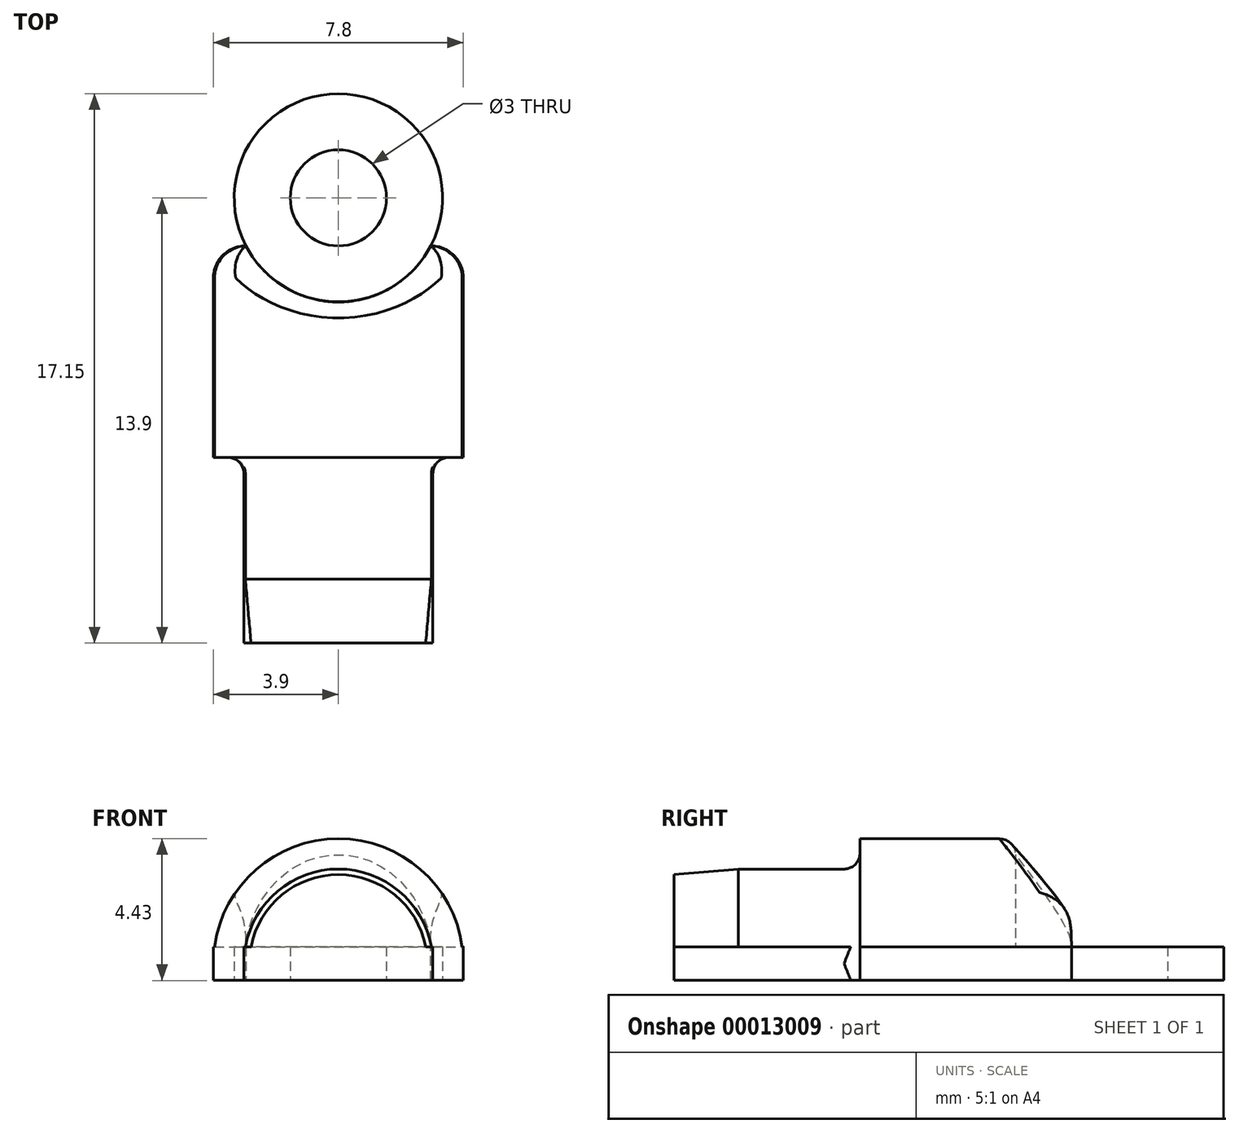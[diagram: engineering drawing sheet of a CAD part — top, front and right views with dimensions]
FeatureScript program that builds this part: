
annotation { "Feature Type Name" : "Feature", "Feature Type Description" : "" }
export const myFeature = defineFeature(function(context is Context, id is Id, definition is map)
    precondition{}
    {
        {
            var Q0;
            Q0=qCreatedBy(makeId("Top.planeOp"),FACE);
            var sketch = newSketch(context, id + "F0", { "sketchPlane" : qUnion([Q0])});
            skArc(sketch, "E0", {"start": v(2.88, -1.5) * mm, "mid": v(0, 3.25) * mm, "end": v(-2.88, -1.5) * mm});
            skCircle(sketch, "E1", {"center": v(0, 0) * mm, "radius": 1.5 * mm});
            skLineSegment(sketch, "E2.bottom", {"start": v(-2.9, -1.5) * mm, "end": v(-2.88, -1.5) * mm});
            skLineSegment(sketch, "E2.top", {"start": v(-3.9, -8.1) * mm, "end": v(-2.95, -8.1) * mm});
            skLineSegment(sketch, "E2.left", {"start": v(-3.9, -2.5) * mm, "end": v(-3.9, -8.1) * mm});
            skLineSegment(sketch, "E2.right", {"start": v(3.9, -2.5) * mm, "end": v(3.9, -8.1) * mm});
            skLineSegment(sketch, "E3.top", {"start": v(-2.95, -13.9) * mm, "end": v(2.95, -13.9) * mm});
            skLineSegment(sketch, "E3.left", {"start": v(-2.95, -8.1) * mm, "end": v(-2.95, -13.9) * mm});
            skLineSegment(sketch, "E3.right", {"start": v(2.95, -8.1) * mm, "end": v(2.95, -13.9) * mm});
            skPoint(sketch, "E4.visualSharp", {"position": v(-3.9, -1.5) * mm});
            skArc(sketch, "E4.filletArc", {"start": v(-2.9, -1.5) * mm, "mid": v(-3.6, -1.8) * mm, "end": v(-3.9, -2.5) * mm});
            skPoint(sketch, "E5.visualSharp", {"position": v(3.9, -1.5) * mm});
            skArc(sketch, "E5.filletArc", {"start": v(3.9, -2.5) * mm, "mid": v(3.6, -1.8) * mm, "end": v(2.9, -1.5) * mm});
            skLineSegment(sketch, "E6.trimOffspring", {"start": v(2.88, -1.5) * mm, "end": v(2.9, -1.5) * mm});
            skLineSegment(sketch, "E7.trimOffspring", {"start": v(2.95, -8.1) * mm, "end": v(3.9, -8.1) * mm});
            skSolve(sketch);
        }
        {
            var Q0;
            Q0=makeQuery(id+"F0.imprint","IMPRINT",FACE,{"disambiguationData":[TD([[makeQuery(id+"F0.imprint","IMPRINT",EDGE,{"derivedFrom":sQuery(id+"F0.wireOp",EDGE,"E0")}),1.0]])]});
            extrude(context, id + "F1", {"entities" : qUnion([Q0]), "endBound" : BoundingType.SYMMETRIC, "depth" : 1.05 * mm});
        }
        {
            var Q0;
            Q0=qCreatedBy(makeId("Top.planeOp"),FACE);
            var sketch = newSketch(context, id + "F2", { "sketchPlane" : qUnion([Q0])});
            skLineSegment(sketch, "E8", {"start": v(0, -13.9) * mm, "end": v(-2.95, -13.9) * mm});
            skLineSegment(sketch, "E9", {"start": v(-2.95, -13.9) * mm, "end": v(-2.95, -8.1) * mm});
            skLineSegment(sketch, "E10", {"start": v(-2.95, -8.1) * mm, "end": v(-3.9, -8.1) * mm});
            skLineSegment(sketch, "E11", {"start": v(-3.9, -8.1) * mm, "end": v(-3.9, -2.5) * mm});
            skLineSegment(sketch, "E12", {"start": v(-2.9, -1.5) * mm, "end": v(-2.9, -1.5) * mm});
            skPoint(sketch, "E13.visualSharp", {"position": v(-3.9, -1.5) * mm});
            skArc(sketch, "E13.filletArc", {"start": v(-2.9, -1.5) * mm, "mid": v(-3.6, -1.8) * mm, "end": v(-3.9, -2.5) * mm});
            skLineSegment(sketch, "E14", {"start": v(0, -1.5) * mm, "end": v(0, -13.9) * mm});
            skPoint(sketch, "E15.orphan", {"position": v(0, -1.5) * mm});
            skLineSegment(sketch, "E16", {"start": v(-2.9, -1.5) * mm, "end": v(0, -1.5) * mm});
            skSolve(sketch);
        }
        {
            var Q0;
            Q0 = qSketchRegion(id + "F2", true);
            var Q1;
            Q1=sQuery(id+"F2.wireOp",EDGE,"E14");
            revolve(context, id + "F3", {"operationType" : NewBodyOperationType.ADD, "entities" : qUnion([Q0]), "axis" : qUnion([Q1]), "revolveType" : RevolveType.ONE_DIRECTION, "oppositeDirection" : true, "angle" : 180 * degree});
        }
        {
            var Q0;
            Q0=makeQuery(id+"F1.opExtrude","CAP_FACE",FACE,{"disambiguationData":[OSD([sQuery(id+"F0.wireOp",EDGE,"E0"),sQuery(id+"F0.wireOp",EDGE,"E1"),sQuery(id+"F0.wireOp",EDGE,"E2.bottom"),sQuery(id+"F0.wireOp",EDGE,"E2.top"),sQuery(id+"F0.wireOp",EDGE,"E2.left"),sQuery(id+"F0.wireOp",EDGE,"E2.right"),sQuery(id+"F0.wireOp",EDGE,"E3.top"),sQuery(id+"F0.wireOp",EDGE,"E3.left"),sQuery(id+"F0.wireOp",EDGE,"E3.right"),sQuery(id+"F0.wireOp",EDGE,"E4.filletArc"),sQuery(id+"F0.wireOp",EDGE,"E5.filletArc"),sQuery(id+"F0.wireOp",EDGE,"E6.trimOffspring"),sQuery(id+"F0.wireOp",EDGE,"E7.trimOffspring")])],"isStart":false});
            var sketch = newSketch(context, id + "F4", { "sketchPlane" : qUnion([Q0])});
            skCircle(sketch, "E17", {"center": v(0, 0) * mm, "radius": 3.25 * mm});
            skSolve(sketch);
        }
        {
            var Q0;
            Q0 = qSketchRegion(id + "F4", true);
            extrude(context, id + "F5", {"entities" : qUnion([Q0]), "operationType" : NewBodyOperationType.REMOVE, "endBound" : BoundingType.THROUGH_ALL, "depth" : 25 * mm});
        }
        {
            var Q0;
            Q0=makeQuery(id+"F5.boolean.opBoolean","INTERSECT",EDGE,{"derivedFrom":[makeQuery(id+"F3.opRevolve","SWEPT_FACE",FACE,{"disambiguationData":[OSD([sQuery(id+"F2.wireOp",EDGE,"E11")])]}),makeQuery(id+"F5.opExtrude","SWEPT_FACE",FACE,{"disambiguationData":[OSD([sQuery(id+"F4.wireOp",EDGE,"E17")])]})]});
            fillet(context, id + "F6", {"entities" : qUnion([Q0]), "radius" : 0.5 * mm, "allowEdgeOverflow" : false});
        }
        {
            var Q0;
            Q0=makeQuery(id+"F3.opRevolve","SWEPT_EDGE",EDGE,{"disambiguationData":[OSD([sQuery(id+"F2.wireOp",EDGE,"E8"),sQuery(id+"F2.wireOp",EDGE,"E9")])]});
            chamfer(context, id + "F7", {"entities" : qUnion([Q0]), "chamferType" : ChamferType.OFFSET_ANGLE, "width" : 2 * mm, "oppositeDirection" : true, "angle" : 5 * degree, "tangentPropagation" : true});
        }
        {
            var Q0;
            Q0=makeQuery(id+"F3.opRevolve","SWEPT_EDGE",EDGE,{"disambiguationData":[OSD([sQuery(id+"F2.wireOp",EDGE,"E9"),sQuery(id+"F2.wireOp",EDGE,"E10")])]});
            fillet(context, id + "F8", {"entities" : qUnion([Q0]), "radius" : 0.5 * mm, "tangentPropagation" : true, "allowEdgeOverflow" : false});
        }
    });
